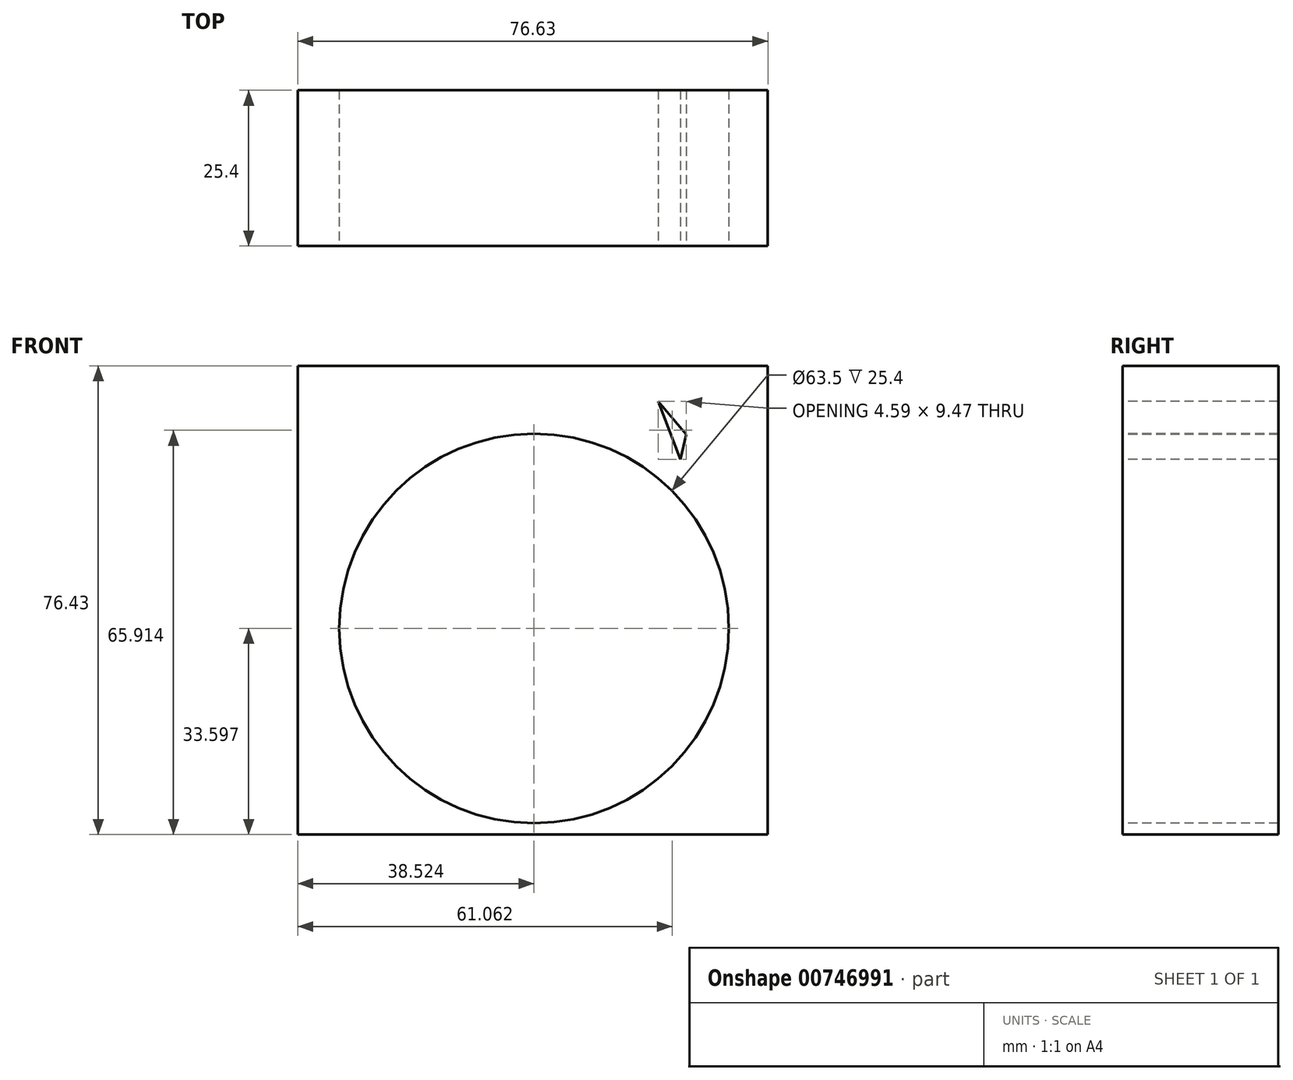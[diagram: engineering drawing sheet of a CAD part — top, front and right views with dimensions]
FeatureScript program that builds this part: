
annotation { "Feature Type Name" : "Feature", "Feature Type Description" : "" }
export const myFeature = defineFeature(function(context is Context, id is Id, definition is map)
    precondition{}
    {
        {
            var Q0;
            Q0=qCreatedBy(makeId("Front.planeOp"),FACE);
            var sketch = newSketch(context, id + "F0", { "sketchPlane" : qUnion([Q0])});
            skLineSegment(sketch, "E0.bottom", {"start": v(0, 0) * mm, "end": v(76.63, 0) * mm});
            skLineSegment(sketch, "E0.top", {"start": v(0, 76.43) * mm, "end": v(76.63, 76.43) * mm});
            skLineSegment(sketch, "E0.left", {"start": v(0, 0) * mm, "end": v(0, 76.43) * mm});
            skLineSegment(sketch, "E0.right", {"start": v(76.63, 0) * mm, "end": v(76.63, 76.43) * mm});
            skSolve(sketch);
        }
        {
            var Q0;
            Q0 = qSketchRegion(id + "F0", true);
            extrude(context, id + "F1", {"entities" : qUnion([Q0]), "depth" : 25.4 * mm, "offsetDistance" : 25.4 * mm});
        }
        {
            var Q0;
            Q0=makeQuery(id+"F1.opExtrude","CAP_FACE",FACE,{"disambiguationData":[OSD([sQuery(id+"F0.wireOp",EDGE,"E0.bottom"),sQuery(id+"F0.wireOp",EDGE,"E0.top"),sQuery(id+"F0.wireOp",EDGE,"E0.left"),sQuery(id+"F0.wireOp",EDGE,"E0.right")])],"isStart":false});
            var sketch = newSketch(context, id + "F2", { "sketchPlane" : qUnion([Q0])});
            skCircle(sketch, "E1", {"center": v(38.52, 33.6) * mm, "radius": 31.75 * mm});
            skSolve(sketch);
        }
        {
            var Q0;
            Q0=makeQuery(id+"F2.imprint","IMPRINT",FACE,{"disambiguationData":[TD([[makeQuery(id+"F2.imprint","IMPRINT",EDGE,{"derivedFrom":sQuery(id+"F2.wireOp",EDGE,"E1")}),1.0]])]});
            extrude(context, id + "F3", {"entities" : qUnion([Q0]), "operationType" : NewBodyOperationType.REMOVE, "endBound" : BoundingType.THROUGH_ALL, "oppositeDirection" : true, "depth" : 25.4 * mm, "offsetDistance" : 25.4 * mm});
        }
        {
            var Q0;
            Q0=makeQuery(id+"F1.opExtrude","CAP_FACE",FACE,{"disambiguationData":[OSD([sQuery(id+"F0.wireOp",EDGE,"E0.bottom"),sQuery(id+"F0.wireOp",EDGE,"E0.top"),sQuery(id+"F0.wireOp",EDGE,"E0.left"),sQuery(id+"F0.wireOp",EDGE,"E0.right")])],"isStart":false});
            var sketch = newSketch(context, id + "F4", { "sketchPlane" : qUnion([Q0])});
            skLineSegment(sketch, "E2", {"start": v(58.77, 70.65) * mm, "end": v(63.36, 65.2) * mm});
            skLineSegment(sketch, "E3", {"start": v(62.38, 61.18) * mm, "end": v(58.77, 70.65) * mm});
            skLineSegment(sketch, "E4", {"start": v(62.38, 61.18) * mm, "end": v(63.36, 65.2) * mm});
            skSolve(sketch);
        }
        {
            var Q0;
            Q0 = qSketchRegion(id + "F4", true);
            extrude(context, id + "F5", {"entities" : qUnion([Q0]), "operationType" : NewBodyOperationType.REMOVE, "oppositeDirection" : true, "depth" : 25.4 * mm, "offsetDistance" : 25.4 * mm});
        }
    });
